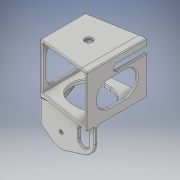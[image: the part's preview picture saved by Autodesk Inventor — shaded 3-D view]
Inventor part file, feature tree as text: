
AUTODESK INVENTOR PART (.ipt)
format: ipt  version: 2018 (Build 220112000, 112)  size: 689,152 bytes
history: native  units: in
note: dims shown in document units (in); Inventor stores cm internally (conversion verified against a paired STEP export)
features: extrude x13, sketch x13, fillet x12, projected_geometry x4, plane x2
ambient origin geometry x8: Origin, YZ Plane, XZ Plane, XY Plane, X Axis, Y Axis, Z Axis, Center Point
bodies: Solid1 (feature_tree)
feature tree (44):
  extrude  "Extrusion1"  Depth=1.3386in TaperAngle=0.0deg
  plane  "Work Plane1"
  extrude  "Extrusion3"  Depth=0.0709in
  extrude  "Extrusion4"  Depth=0.1575in
  extrude  "Extrusion6"  Depth=0.1181in
  extrude  "Extrusion7"  Depth=0.0984in
  extrude  "Extrusion8"  Depth=0.5906in TaperAngle=0.0deg
  extrude  "Extrusion9"  TaperAngle=0.0deg  [1 undecoded]
  plane  "Work Plane2"
  extrude  "Extrusion11"  Depth=1.2598in
  extrude  "Extrusion12"  Depth=0.9843in TaperAngle=0.0deg
  extrude  "Extrusion15"  Depth=1.0236in
  extrude  "Extrusion16"  Depth=0.0591in
  fillet  "Fillet32"  Radius=0.0197in
  extrude  "Extrusion18"  Depth=0.3937in TaperAngle=0.0deg
  fillet  "Fillet33"  Radius=0.1969in
  fillet  "Fillet34"  Radius=0.6693in
  fillet  "Fillet35"  Radius=0.1772in
  fillet  "Fillet36"  Radius=0.1969in
  fillet  "Fillet37"  Radius=0.3937in
  fillet  "Fillet38"  Radius=1.0in
  fillet  "Fillet39"  Radius=0.0197in
  fillet  "Fillet40"  Radius=0.0197in
  fillet  "Fillet41"  Radius=0.0197in
  fillet  "Fillet42"  Radius=0.0197in
  extrude  "Extrusion20"  Depth=0.0157in
  fillet  "Fillet44"  Radius=0.0197in
  sketch  "Sketch1"  dims[d4=0.5906in d5=1.3386in d6=0.0in]
  sketch  "Sketch3"  dims[d21=3.937in d22=0.0in d23=0.0709in]
  projected_geometry  "Projected Loop2"
  sketch  "Sketch4"  dims[d24=3.937in d25=0.0in d34=0.1575in]
  projected_geometry  "Projected Loop3"
  sketch  "Sketch7"  dims[d36=3.937in d37=0.0in d39=0.1181in]
  projected_geometry  "Projected Loop5"
  sketch  "Sketch8"  dims[d42=0.0984in d43=0.0984in]
  sketch  "Sketch9"  dims[d44=0.1969in d45=0.5906in d46=0.0in]
  sketch  "Sketch10"  dims[d47=0.0787in d48=0.0in]
  sketch  "Sketch14"  dims[d49=1.1811in d50=1.2598in]
  sketch  "Sketch16"  dims[d51=0.9843in d52=0.0in d57=0.9843in d58=0.0in]
  sketch  "Sketch20"  dims[d60=-1.4173in d66=1.0236in]
  sketch  "Sketch21"  dims[d68=0.1969in d69=0.0in d78=0.0591in d79=0.0197in]
  projected_geometry  "Projected Loop7"
  sketch  "Sketch24"  dims[d80=0.0591in d81=0.0591in d82=0.0in d92=0.1969in d93=0.0in d94=0.6693in d95=0.1772in d96=0.1969in d97=0.0in d144=0.3937in d145=1.0in d146=0.0in d147=0.0197in d148=0.0197in d149=0.0197in d150=0.0197in]
  sketch  "Sketch25"  dims[d151=0.0197in d152=0.0197in d153=0.0197in d154=0.0157in d155=0.0157in d156=0.0157in d163=0.0394in d164=0.0787in d165=0.3937in d166=0.0in d167=0.0157in]
note: 1 required parameter value undecoded (feature->parameter linkage not recoverable at this tier; creation-order binding heuristic only, values carry confidence <= 0.55)
